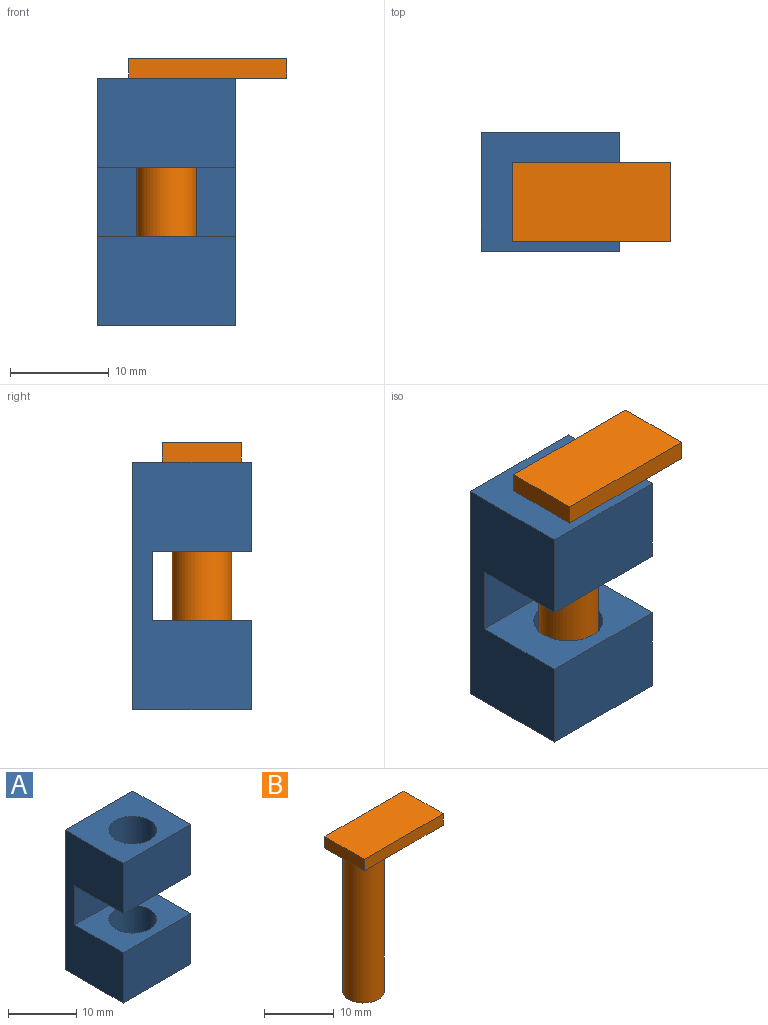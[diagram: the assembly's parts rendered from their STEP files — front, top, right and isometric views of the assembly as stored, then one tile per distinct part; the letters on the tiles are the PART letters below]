
ASSEMBLY  parts=2 mates=1
PART A: 12 faces, bbox 14x12x25 mm
  f0: plane 14x9mm, normal (0,-1,0), area 126mm2, adj f1,f4,f6,f9
  f1: plane 25x12mm, normal (1,0,0), area 230mm2, adj f0,f3,f5,f6,f7,f9,f10,f11
  f2: cylinder r=3.5mm len=9mm, axis (0,0,-1), area 197.9mm2, adj f7,f10
  f3: plane 25x14mm, normal (0,1,0), area 350mm2, adj f1,f4,f6,f7
  f4: plane 25x12mm, normal (-1,0,0), area 230mm2, adj f0,f3,f5,f6,f7,f9,f10,f11
  f5: plane 14x9mm, normal (0,-1,0), area 126mm2, adj f1,f4,f7,f10
  f6: plane 14x12mm, normal (0,0,1), area 129.5mm2, adj f0,f1,f3,f4,f8
  f7: plane 14x12mm, normal (0,0,-1), area 129.5mm2, adj f1,f2,f3,f4,f5
  f8: cylinder r=3.5mm len=9mm, axis (0,0,-1), area 197.9mm2, adj f6,f9
  f9: plane 14x10mm, normal (0,0,-1), area 101.5mm2, adj f0,f1,f4,f8,f11
  f10: plane 14x10mm, normal (0,0,1), area 101.5mm2, adj f1,f2,f4,f5,f11
  f11: plane 14x7mm, normal (0,-1,0), area 98mm2, adj f1,f4,f9,f10
PART B: 8 faces, bbox 16x8x27 mm
  f0: plane 16x2mm, normal (0,1,0), area 32mm2, adj f1,f3,f4,f7
  f1: plane 8x2mm, normal (-1,0,0), area 16mm2, adj f0,f2,f3,f4
  f2: plane 16x2mm, normal (0,-1,0), area 32mm2, adj f1,f3,f4,f7
  f3: plane 16x8mm, normal (0,0,1), area 128mm2, adj f0,f1,f2,f7
  f4: plane 16x8mm, normal (0,0,-1), area 99.7mm2, adj f0,f1,f2,f5,f7
  f5: cylinder r=3mm len=25mm, axis (0,0,1), area 471.2mm2, adj f4,f6
  f6: plane 6x6mm, normal (0,0,-1), area 28.3mm2, adj f5
  f7: plane 8x2mm, normal (1,0,0), area 16mm2, adj f0,f2,f3,f4
PLACE A at identity
PLACE B t=(2.17,-1,25)mm
MATE fastened B.f5 <-> A.f2  axis (0,0,-1) through (0,-1,0)mm
